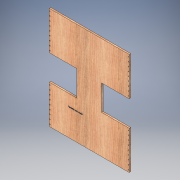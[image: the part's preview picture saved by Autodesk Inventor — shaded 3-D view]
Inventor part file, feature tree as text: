
AUTODESK INVENTOR PART (.ipt)
format: ipt  version: 2018 (Build 220112000, 112)  size: 695,296 bytes
history: native  units: in
note: dims shown in document units (in); Inventor stores cm internally (conversion verified against a paired STEP export)
features: extrude x3, sketch x3
ambient origin geometry x8: Origin, YZ Plane, XZ Plane, XY Plane, X Axis, Y Axis, Z Axis, Center Point
bodies: Solid1 (feature_tree)
feature tree (6):
  extrude  "Extrusion1"  Depth=9.0in
  extrude  "Extrusion2"  Depth=6.0in
  extrude  "Extrusion3"  Depth=6.5in
  sketch  "Sketch1"  dims[d0=18.75in d1=9.0in]
  sketch  "Sketch2"  dims[d2=6.5in d3=6.0in]
  sketch  "Sketch3"  dims[d4=9.0in d5=6.5in d6=0.375in d7=0.0in d8=0.125in d9=0.5in d10=1.0in d11=1.0in d12=1.0in d13=1.0in d14=1.0in d15=1.0in d16=1.0in d17=1.0in d18=0.2031in d19=3.25in d20=0.0in d21=1.0in d22=0.0in]
